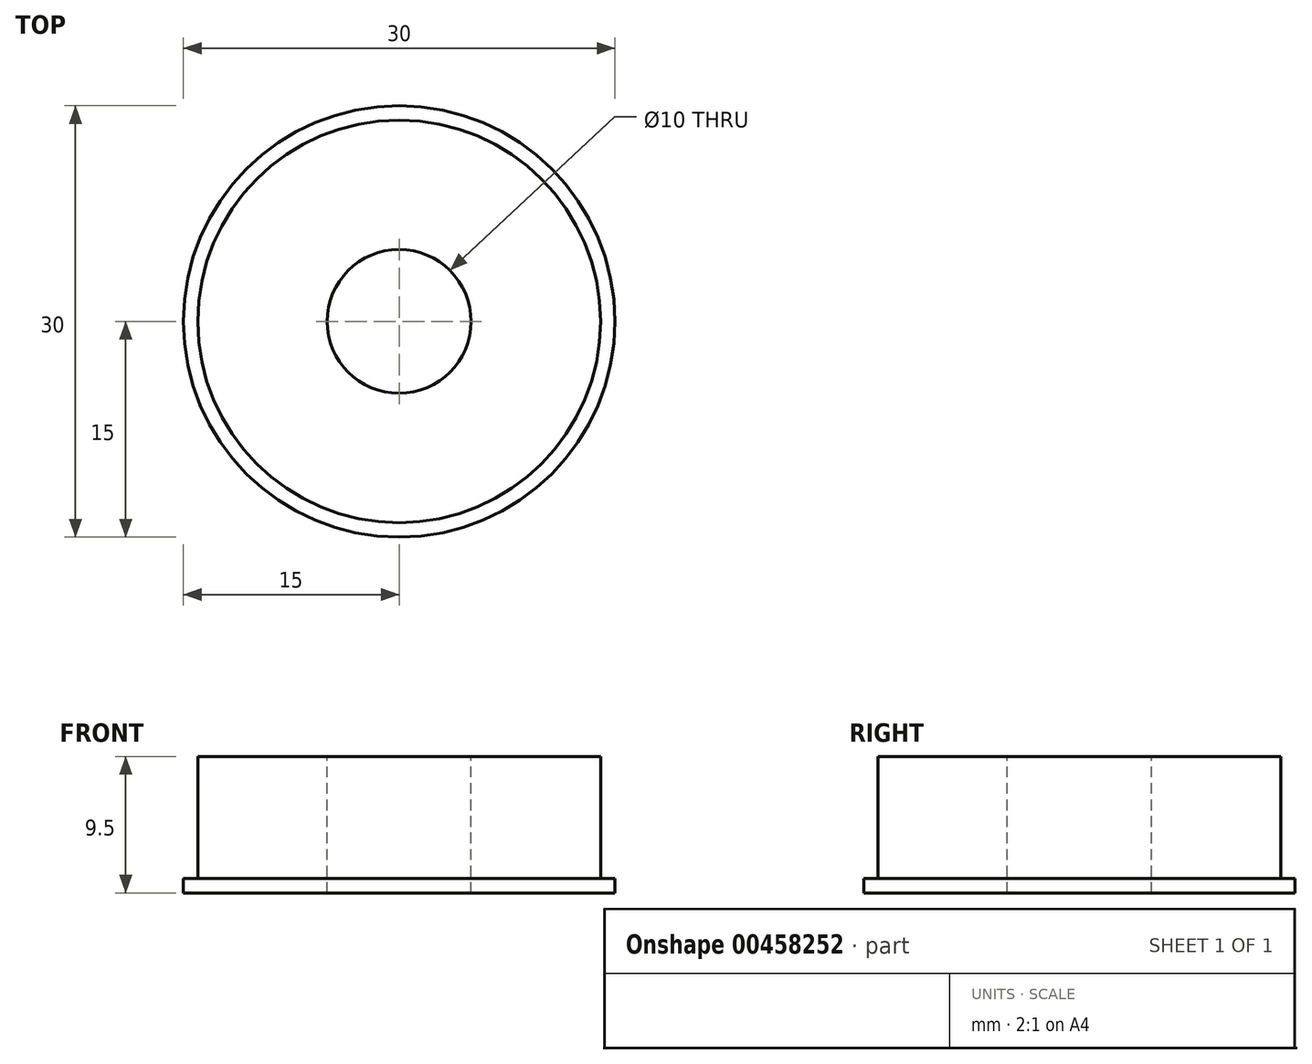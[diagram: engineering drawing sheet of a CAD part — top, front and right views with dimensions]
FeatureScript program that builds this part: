
annotation { "Feature Type Name" : "Feature", "Feature Type Description" : "" }
export const myFeature = defineFeature(function(context is Context, id is Id, definition is map)
    precondition{}
    {
        {
            var Q0;
            Q0=qCreatedBy(makeId("Top.planeOp"),FACE);
            var sketch = newSketch(context, id + "F0", { "sketchPlane" : qUnion([Q0])});
            skCircle(sketch, "E0", {"center": v(0, 0) * mm, "radius": 15 * mm});
            skSolve(sketch);
        }
        {
            var Q0;
            Q0 = qSketchRegion(id + "F0", true);
            extrude(context, id + "F1", {"entities" : qUnion([Q0]), "depth" : 1 * mm});
        }
        {
            var Q0;
            Q0=makeQuery(id+"F1.opExtrude","CAP_FACE",FACE,{"disambiguationData":[OSD([sQuery(id+"F0.wireOp",EDGE,"E0")])],"isStart":false});
            var sketch = newSketch(context, id + "F2", { "sketchPlane" : qUnion([Q0])});
            skCircle(sketch, "E1", {"center": v(0, 0) * mm, "radius": 14 * mm});
            skSolve(sketch);
        }
        {
            var Q0;
            Q0 = qSketchRegion(id + "F2", true);
            extrude(context, id + "F3", {"entities" : qUnion([Q0]), "operationType" : NewBodyOperationType.ADD, "depth" : 8.5 * mm});
        }
        {
            var Q0;
            Q0=makeQuery(id+"F3.opExtrude","CAP_FACE",FACE,{"disambiguationData":[OSD([sQuery(id+"F2.wireOp",EDGE,"E1")])],"isStart":false});
            var sketch = newSketch(context, id + "F4", { "sketchPlane" : qUnion([Q0])});
            skCircle(sketch, "E2", {"center": v(0, 0) * mm, "radius": 5 * mm});
            skSolve(sketch);
        }
        {
            var Q0;
            Q0 = qSketchRegion(id + "F4", true);
            var Q1;
            Q1=makeQuery(id+"F1.opExtrude","CAP_FACE",FACE,{"disambiguationData":[OSD([sQuery(id+"F0.wireOp",EDGE,"E0")])],"isStart":true});
            extrude(context, id + "F5", {"entities" : qUnion([Q0]), "operationType" : NewBodyOperationType.REMOVE, "endBound" : BoundingType.UP_TO_SURFACE, "oppositeDirection" : true, "endBoundEntityFace" : qUnion([Q1]), "depth" : 25 * mm});
        }
    });
